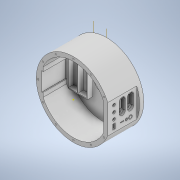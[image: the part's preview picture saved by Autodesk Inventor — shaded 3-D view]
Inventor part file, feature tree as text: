
AUTODESK INVENTOR PART (.ipt)
format: ipt  version: 2020.3 (Build 243373000, 373)  size: 481,280 bytes
history: native  units: mm
features: sketch x23, extrude x21, pattern_linear x3, other x3, pattern_circular x1
ambient origin geometry x8: Origin, YZ Plane, XZ Plane, XY Plane, X Axis, Y Axis, Z Axis, Center Point
bodies: Solid1 (feature_tree)
feature tree (51):
  extrude  "Extrusion1"  Depth=10.0mm TaperAngle=0.0deg
  extrude  "Extrusion2"  Depth=70.0mm
  extrude  "Extrusion4"  Depth=10.0mm
  extrude  "Extrusion7"  Depth=10.0mm TaperAngle=0.0deg
  extrude  "Extrusion8"  Depth=5.9mm
  extrude  "Extrusion9"  Depth=7.0mm
  pattern_linear  "Rectangular Pattern1"  Count1=2  [1 undecoded]
  sketch  "Sketch12"  dims[d36=12.6mm d37=7.0mm]
  extrude  "Extrusion10"  Depth=14.8mm
  extrude  "Extrusion11"  Depth=24.0mm
  extrude  "Extrusion12"  Depth=5.0mm TaperAngle=0.0deg
  extrude  "Extrusion13"  Depth=2.7mm
  extrude  "Extrusion14"  Depth=10.0mm TaperAngle=0.0deg
  extrude  "Extrusion15"  Depth=6.0mm
  extrude  "Extrusion16"  Depth=6.5mm
  extrude  "Extrusion17"  Depth=6.0mm
  pattern_circular  "Circular Pattern2"  [2 undecoded]
  extrude  "Extrusion18"  Depth=10.0mm
  extrude  "Extrusion19"  Depth=10.0mm
  pattern_linear  "Rectangular Pattern2"  Spacing1=10.0mm  [1 undecoded]
  extrude  "Extrusion20"  Depth=7.0mm TaperAngle=0.0deg
  extrude  "Extrusion21"  Depth=1.5mm
  sketch  "Sketch28"  dims[d58=2.7mm d59=10.0mm d60=0.0mm]
  extrude  "Extrusion23"  Depth=8.0mm
  extrude  "Extrusion24"  Depth=7.0mm
  extrude  "Extrusion25"  Depth=9.0mm
  pattern_linear  "Rectangular Pattern3"  Spacing1=10.0mm  [1 undecoded]
  sketch  "Sketch32"  dims[d70=6.0mm d71=5.0mm d72=0.0mm d73=10.0mm d74=10.0mm d75=10.0mm d76=7.0mm d77=0.0mm d78=1.5mm d79=8.0mm d80=7.0mm d81=9.0mm d82=10.0mm d83=10.0mm d84=1.0mm d85=0.0mm d86=21.2mm d87=21.2mm d88=75.6mm d89=75.6mm d90=2.0mm d91=2.0mm d92=2.0mm d93=2.0mm d94=2.0mm d95=23.0mm d96=13.0mm d97=0.0mm d98=2.0mm d99=1.5mm d100=1.5mm d101=2.0mm d102=1.5mm d103=1.5mm d104=2.0mm d105=0.0mm d106=2.0mm d107=2.0mm d108=1.5mm d109=1.5mm d110=1.5mm d111=1.5mm d112=2.0mm d113=0.0mm d114=85.0mm d115=3.2mm d116=30.0deg d117=100.0mm d118=0.0mm d122=6.0mm d123=54.0mm d124=0.0mm d125=110.0mm d126=300.0deg d128=2.7mm d129=54.0mm d130=4.0mm d131=21.2mm d132=75.6mm d134=2.0mm d135=2.0mm d136=2.0mm d137=2.0mm d138=23.0mm d139=10.0mm d140=0.0mm d141=1.6mm d142=4.0mm d143=15.5mm d144=15.5mm d145=10.0mm d146=0.0mm d147=20.0mm d149=31.0mm d150=20.0mm d152=31.0mm d153=2.0mm d154=1.5mm d155=1.5mm d156=10.0mm d157=0.0mm d158=2.0mm d159=1.5mm d160=1.5mm d161=10.0mm d162=0.0mm d176=45.3mm d177=1.4mm d178=2.0mm d179=1.0mm d180=1.0mm d181=1.4mm d182=2.0mm d183=10.0mm d184=0.0mm d185=10.0mm d186=0.0mm d187=3.5mm d188=4.0mm d189=0.0mm d190=20.0mm d192=31.0mm d193=20.0mm d195=31.0mm]
  sketch  "Sketch1"  dims[d0=180.0mm d1=10.0mm d2=0.0mm]
  sketch  "Sketch2"  dims[d3=42.0mm d4=70.0mm]
  sketch  "Sketch8"  dims[d5=90.0mm d7=10.0mm]
  sketch  "Sketch9"  dims[d8=70.0mm d9=0.0mm d20=10.0mm d21=0.0mm]
  sketch  "Sketch11"  dims[d34=10.0mm d35=5.9mm]
  sketch  "Sketch13"  dims[d38=7.0mm]
  sketch  "Sketch14"  dims[d39=7.0mm]
  sketch  "Sketch15"  dims[d41=15.0mm]
  sketch  "Sketch16"  dims[d42=15.0mm]
  sketch  "Sketch17"  dims[d43=15.0mm]
  sketch  "Sketch18"  dims[d44=12.5mm]
  sketch  "Sketch19"  dims[d45=15.0mm]
  sketch  "Sketch20"  dims[d46=2.95mm d47=20.0mm]
  sketch  "Sketch22"  dims[d48=10.0mm d49=0.0mm d50=14.8mm]
  sketch  "Sketch23"  dims[d51=24.0mm d52=25.0mm]
  sketch  "Sketch24"  dims[d53=20.0mm d54=5.0mm d55=0.0mm]
  sketch  "Sketch25"  dims[d56=29.0mm d57=2.7mm]
  sketch  "Sketch29"  dims[d61=20.0mm d63=20.0mm d64=6.0mm]
  sketch  "Sketch30"  dims[d66=30.0mm d67=6.5mm]
  sketch  "Sketch31"  dims[d68=6.5mm d69=6.0mm]
  other  "Work Axis1"
  other  "Work Axis2"
  other  "Work Axis3"
note: 5 required parameter values undecoded (feature->parameter linkage not recoverable at this tier; creation-order binding heuristic only, values carry confidence <= 0.55)
